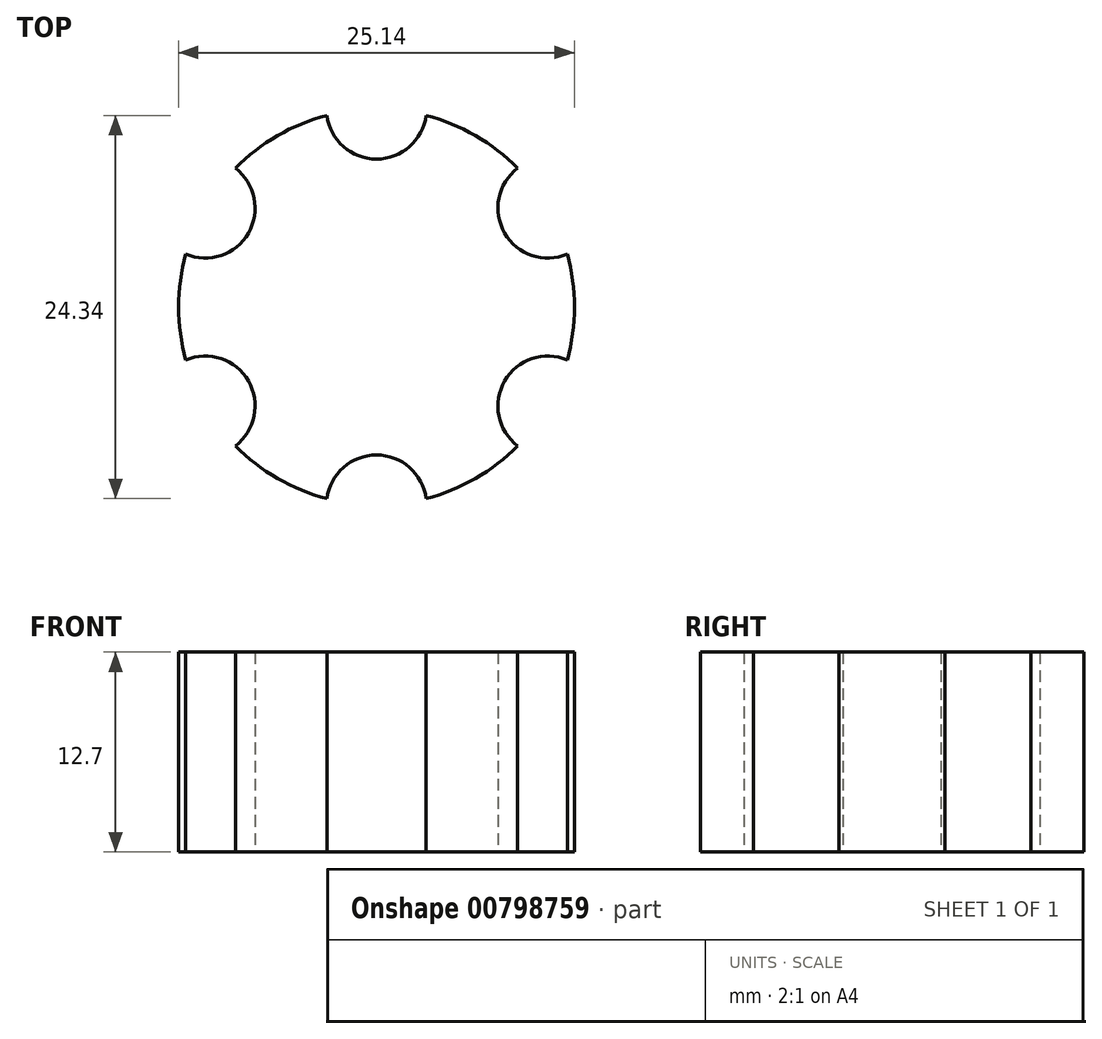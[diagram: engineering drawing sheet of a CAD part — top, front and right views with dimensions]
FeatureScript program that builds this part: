
annotation { "Feature Type Name" : "Feature", "Feature Type Description" : "" }
export const myFeature = defineFeature(function(context is Context, id is Id, definition is map)
    precondition{}
    {
        {
            var Q0;
            Q0=qCreatedBy(makeId("Top.planeOp"),FACE);
            var sketch = newSketch(context, id + "F0", { "sketchPlane" : qUnion([Q0])});
            skArc(sketch, "E0", {"start": v(-3.15, 12.17) * mm, "mid": v(-6.29, 10.89) * mm, "end": v(-8.97, 8.81) * mm});
            skLineSegment(sketch, "E1.0", {"start": v(0, 12.57) * mm, "end": v(10.89, 6.29) * mm, "construction": true});
            skLineSegment(sketch, "E1.1", {"start": v(10.89, 6.29) * mm, "end": v(10.89, -6.29) * mm, "construction": true});
            skLineSegment(sketch, "E1.2", {"start": v(10.89, -6.29) * mm, "end": v(0, -12.57) * mm, "construction": true});
            skLineSegment(sketch, "E1.3", {"start": v(0, -12.57) * mm, "end": v(-10.89, -6.29) * mm, "construction": true});
            skLineSegment(sketch, "E1.4", {"start": v(-10.89, -6.29) * mm, "end": v(-10.89, 6.29) * mm, "construction": true});
            skLineSegment(sketch, "E1.5", {"start": v(-10.89, 6.29) * mm, "end": v(0, 12.57) * mm, "construction": true});
            skArc(sketch, "E2", {"start": v(-3.15, 12.17) * mm, "mid": v(0, 9.4) * mm, "end": v(3.15, 12.17) * mm});
            skArc(sketch, "E3", {"start": v(8.97, 8.81) * mm, "mid": v(8.14, 4.7) * mm, "end": v(12.12, 3.36) * mm});
            skArc(sketch, "E4", {"start": v(12.12, -3.36) * mm, "mid": v(8.14, -4.7) * mm, "end": v(8.97, -8.81) * mm});
            skArc(sketch, "E5", {"start": v(3.15, -12.17) * mm, "mid": v(0, -9.4) * mm, "end": v(-3.15, -12.17) * mm});
            skArc(sketch, "E6", {"start": v(-8.97, -8.81) * mm, "mid": v(-8.14, -4.7) * mm, "end": v(-12.12, -3.36) * mm});
            skArc(sketch, "E7", {"start": v(-12.12, 3.36) * mm, "mid": v(-8.14, 4.7) * mm, "end": v(-8.97, 8.81) * mm});
            skArc(sketch, "E8.trimOffspring", {"start": v(8.97, 8.81) * mm, "mid": v(6.29, 10.89) * mm, "end": v(3.15, 12.17) * mm});
            skArc(sketch, "E9.trimOffspring", {"start": v(12.12, -3.36) * mm, "mid": v(12.57, 0) * mm, "end": v(12.12, 3.36) * mm});
            skArc(sketch, "E10.trimOffspring", {"start": v(3.15, -12.17) * mm, "mid": v(6.29, -10.89) * mm, "end": v(8.97, -8.81) * mm});
            skArc(sketch, "E11.trimOffspring", {"start": v(-8.97, -8.81) * mm, "mid": v(-6.29, -10.89) * mm, "end": v(-3.15, -12.17) * mm});
            skArc(sketch, "E12.trimOffspring", {"start": v(-12.12, 3.36) * mm, "mid": v(-12.57, 0) * mm, "end": v(-12.12, -3.36) * mm});
            skSolve(sketch);
        }
        {
            var Q0;
            Q0=makeQuery(id+"F0.imprint","IMPRINT",FACE,{"disambiguationData":[TD([[makeQuery(id+"F0.imprint","IMPRINT",EDGE,{"derivedFrom":sQuery(id+"F0.wireOp",EDGE,"E0")}),1.0]])]});
            extrude(context, id + "F1", {"entities" : qUnion([Q0]), "depth" : 12.7 * mm, "offsetDistance" : 25.4 * mm});
        }
    });
